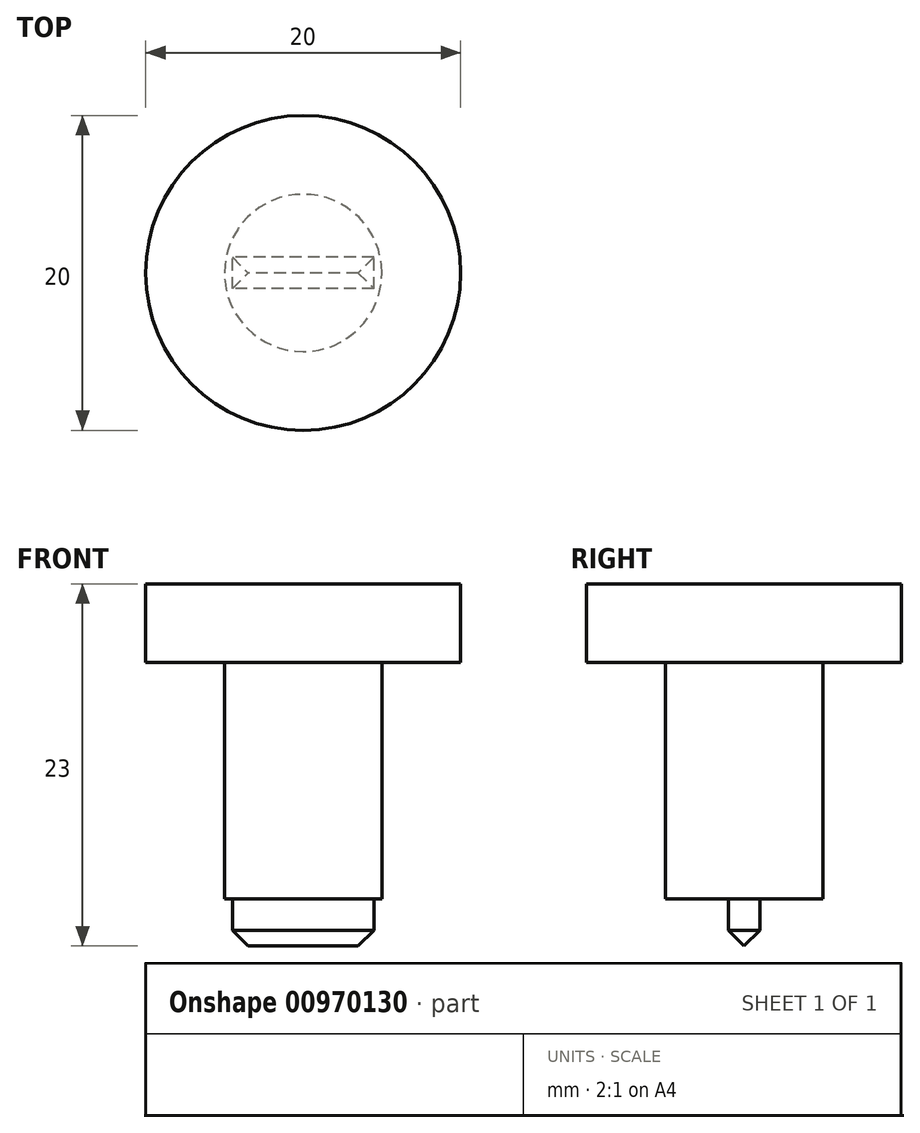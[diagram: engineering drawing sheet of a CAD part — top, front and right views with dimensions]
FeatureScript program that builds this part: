
annotation { "Feature Type Name" : "Feature", "Feature Type Description" : "" }
export const myFeature = defineFeature(function(context is Context, id is Id, definition is map)
    precondition{}
    {
        {
            var Q0;
            Q0=qCreatedBy(makeId("Top.planeOp"),FACE);
            var sketch = newSketch(context, id + "F0", { "sketchPlane" : qUnion([Q0])});
            skCircle(sketch, "E0", {"center": v(0, 0) * mm, "radius": 10 * mm});
            skSolve(sketch);
        }
        {
            var Q0;
            Q0=makeQuery(id+"F0.imprint","IMPRINT",FACE,{"disambiguationData":[TD([[makeQuery(id+"F0.imprint","IMPRINT",EDGE,{"derivedFrom":sQuery(id+"F0.wireOp",EDGE,"E0")}),1.0]])]});
            extrude(context, id + "F1", {"entities" : qUnion([Q0]), "oppositeDirection" : true, "depth" : 5 * mm, "offsetDistance" : 25 * mm});
        }
        {
            var Q0;
            Q0=makeQuery(id+"F1.opExtrude","CAP_FACE",FACE,{"disambiguationData":[OSD([sQuery(id+"F0.wireOp",EDGE,"E0")])],"isStart":false});
            var sketch = newSketch(context, id + "F2", { "sketchPlane" : qUnion([Q0])});
            skCircle(sketch, "E1", {"center": v(0, 0) * mm, "radius": 5 * mm});
            skSolve(sketch);
        }
        {
            var Q0;
            Q0=makeQuery(id+"F2.imprint","IMPRINT",FACE,{"disambiguationData":[TD([[makeQuery(id+"F2.imprint","IMPRINT",EDGE,{"derivedFrom":sQuery(id+"F2.wireOp",EDGE,"E1")}),1.0]])]});
            extrude(context, id + "F3", {"entities" : qUnion([Q0]), "operationType" : NewBodyOperationType.ADD, "depth" : 15 * mm, "offsetDistance" : 25 * mm});
        }
        {
            var Q0;
            Q0=makeQuery(id+"F3.opExtrude","CAP_FACE",FACE,{"disambiguationData":[OSD([sQuery(id+"F2.wireOp",EDGE,"E1")])],"isStart":false});
            var sketch = newSketch(context, id + "F4", { "sketchPlane" : qUnion([Q0])});
            skLineSegment(sketch, "E2.bottom", {"start": v(4.5, 1) * mm, "end": v(-4.5, 1) * mm});
            skLineSegment(sketch, "E2.top", {"start": v(4.5, -1) * mm, "end": v(-4.5, -1) * mm});
            skLineSegment(sketch, "E2.left", {"start": v(4.5, 1) * mm, "end": v(4.5, -1) * mm});
            skLineSegment(sketch, "E2.right", {"start": v(-4.5, 1) * mm, "end": v(-4.5, -1) * mm});
            skPoint(sketch, "E2.middle", {"position": v(0, 0) * mm});
            skSolve(sketch);
        }
        {
            var Q0;
            {var subQ0=sQuery(id+"F4.wireOp",EDGE,"E2.bottom");var subQ1=makeQuery(id+"F3.opExtrude","CAP_EDGE",EDGE,{"disambiguationData":[OSD([sQuery(id+"F2.wireOp",EDGE,"E1")])],"isStart":false});var subQ4=makeQuery(id+"F4.imprint","INTERSECT",VERTEX,{"disambiguationData":[OD(0.0)],"derivedFrom":[subQ1,subQ0]});Q0=makeQuery(id+"F4.imprint","IMPRINT",FACE,{"disambiguationData":[TD([[makeQuery(id+"F4.imprint","IMPRINT",EDGE,{"disambiguationData":[TD([[subQ4,-1.0]])],"derivedFrom":subQ0}),1.0]])]});}
            extrude(context, id + "F5", {"entities" : qUnion([Q0]), "operationType" : NewBodyOperationType.ADD, "depth" : 3 * mm, "offsetDistance" : 25 * mm});
        }
        {
            var Q0;
            Q0=makeQuery(id+"F5.opExtrude","CAP_EDGE",EDGE,{"disambiguationData":[OSD([sQuery(id+"F4.wireOp",EDGE,"E2.bottom")])],"isStart":false});
            var Q1;
            Q1=makeQuery(id+"F5.opExtrude","CAP_EDGE",EDGE,{"disambiguationData":[OSD([sQuery(id+"F4.wireOp",EDGE,"E2.right")])],"isStart":false});
            var Q2;
            Q2=makeQuery(id+"F5.opExtrude","CAP_EDGE",EDGE,{"disambiguationData":[OSD([sQuery(id+"F4.wireOp",EDGE,"E2.top")])],"isStart":false});
            var Q3;
            Q3=makeQuery(id+"F5.opExtrude","CAP_EDGE",EDGE,{"disambiguationData":[OSD([sQuery(id+"F4.wireOp",EDGE,"E2.left")])],"isStart":false});
            chamfer(context, id + "F6", {"entities" : qUnion([Q0, Q1, Q2, Q3]), "width" : 1 * mm, "tangentPropagation" : true});
        }
    });
